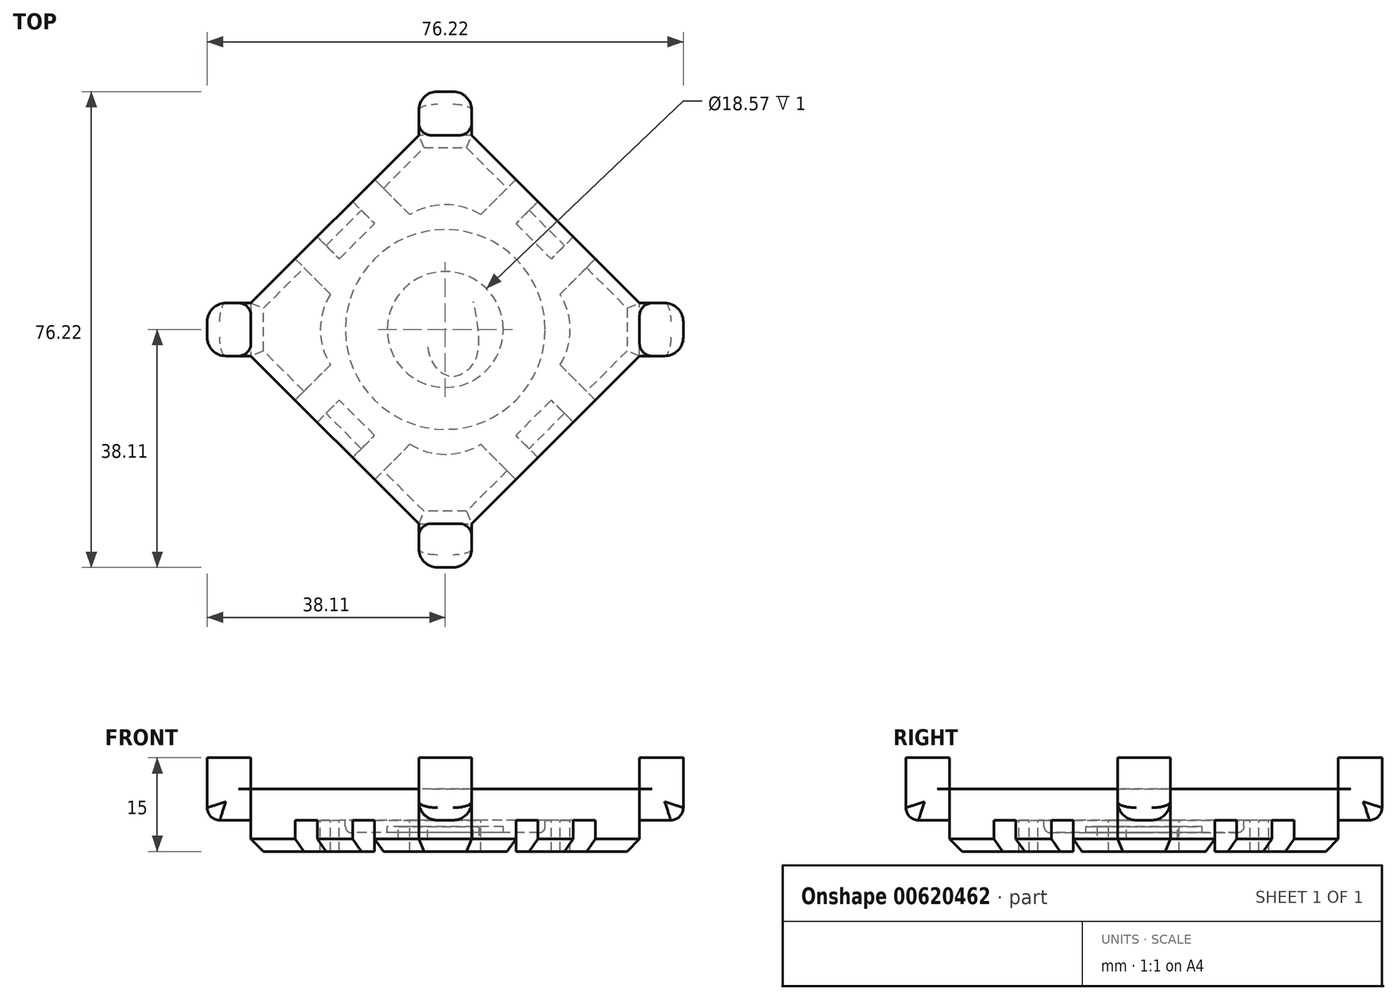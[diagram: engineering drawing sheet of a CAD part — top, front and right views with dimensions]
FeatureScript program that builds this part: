
annotation { "Feature Type Name" : "Feature", "Feature Type Description" : "" }
export const myFeature = defineFeature(function(context is Context, id is Id, definition is map)
    precondition{}
    {
        {
            var Q0;
            Q0=qCreatedBy(makeId("Top.planeOp"),FACE);
            var sketch = newSketch(context, id + "F0", { "sketchPlane" : qUnion([Q0])});
            skLineSegment(sketch, "E0", {"start": v(0, 35.36) * mm, "end": v(0, -35.4) * mm, "construction": true});
            skLineSegment(sketch, "E1", {"start": v(-35.36, 0) * mm, "end": v(35.4, 0) * mm, "construction": true});
            skPoint(sketch, "E2", {"position": v(0, 27.5) * mm});
            skPoint(sketch, "E3", {"position": v(-27.5, 0) * mm});
            skPoint(sketch, "E4", {"position": v(0, -27.5) * mm});
            skPoint(sketch, "E5", {"position": v(27.5, 0) * mm});
            skPoint(sketch, "E6", {"position": v(0, 0) * mm});
            skPoint(sketch, "E7", {"position": v(4.24, 31.11) * mm});
            skPoint(sketch, "E8", {"position": v(-4.24, 31.11) * mm});
            skPoint(sketch, "E9", {"position": v(31.11, 4.24) * mm});
            skPoint(sketch, "E10", {"position": v(31.11, -4.24) * mm});
            skPoint(sketch, "E11", {"position": v(-31.11, -4.24) * mm});
            skPoint(sketch, "E12", {"position": v(-31.11, 4.24) * mm});
            skPoint(sketch, "E13", {"position": v(4.24, -31.11) * mm});
            skPoint(sketch, "E14", {"position": v(-4.24, -31.11) * mm});
            skLineSegment(sketch, "E15", {"start": v(-31.11, 4.24) * mm, "end": v(-4.24, 31.11) * mm});
            skLineSegment(sketch, "E16", {"start": v(4.24, 31.11) * mm, "end": v(31.11, 4.24) * mm});
            skLineSegment(sketch, "E17", {"start": v(31.11, -4.24) * mm, "end": v(4.24, -31.11) * mm});
            skLineSegment(sketch, "E18", {"start": v(-4.24, -31.11) * mm, "end": v(-31.11, -4.24) * mm});
            skLineSegment(sketch, "E19", {"start": v(31.11, 4.24) * mm, "end": v(38.11, 4.24) * mm});
            skLineSegment(sketch, "E20", {"start": v(38.11, 4.24) * mm, "end": v(38.11, -4.24) * mm});
            skLineSegment(sketch, "E21", {"start": v(38.11, -4.24) * mm, "end": v(31.11, -4.24) * mm});
            skLineSegment(sketch, "E22", {"start": v(4.24, -31.11) * mm, "end": v(4.24, -38.11) * mm});
            skLineSegment(sketch, "E23", {"start": v(4.24, -38.11) * mm, "end": v(-4.24, -38.11) * mm});
            skLineSegment(sketch, "E24", {"start": v(-4.24, -38.11) * mm, "end": v(-4.24, -31.11) * mm});
            skLineSegment(sketch, "E25", {"start": v(-31.11, -4.24) * mm, "end": v(-38.11, -4.24) * mm});
            skLineSegment(sketch, "E26", {"start": v(-38.11, -4.24) * mm, "end": v(-38.11, 4.24) * mm});
            skLineSegment(sketch, "E27", {"start": v(-38.11, 4.24) * mm, "end": v(-31.11, 4.24) * mm});
            skLineSegment(sketch, "E28", {"start": v(-4.24, 31.11) * mm, "end": v(-4.24, 38.11) * mm});
            skLineSegment(sketch, "E29", {"start": v(-4.24, 38.11) * mm, "end": v(4.24, 38.11) * mm});
            skLineSegment(sketch, "E30", {"start": v(4.24, 38.11) * mm, "end": v(4.24, 31.11) * mm});
            skLineSegment(sketch, "E31", {"start": v(-4.24, -31.11) * mm, "end": v(4.24, -31.11) * mm});
            skLineSegment(sketch, "E32", {"start": v(31.11, -4.24) * mm, "end": v(31.11, 4.24) * mm});
            skLineSegment(sketch, "E33", {"start": v(4.24, 31.11) * mm, "end": v(-4.24, 31.11) * mm});
            skLineSegment(sketch, "E34", {"start": v(-31.11, 4.24) * mm, "end": v(-31.11, -4.24) * mm});
            skPoint(sketch, "E35", {"position": v(11.31, 24.04) * mm});
            skPoint(sketch, "E36", {"position": v(14.85, 20.5) * mm});
            skPoint(sketch, "E37", {"position": v(20.5, 14.85) * mm});
            skPoint(sketch, "E38", {"position": v(24.04, 11.31) * mm});
            skPoint(sketch, "E39", {"position": v(-24.04, -11.31) * mm});
            skPoint(sketch, "E40", {"position": v(-20.5, -14.85) * mm});
            skPoint(sketch, "E41", {"position": v(-14.85, -20.5) * mm});
            skPoint(sketch, "E42", {"position": v(-11.31, -24.04) * mm});
            skPoint(sketch, "E43", {"position": v(11.31, -24.04) * mm});
            skPoint(sketch, "E44", {"position": v(14.85, -20.5) * mm});
            skPoint(sketch, "E45", {"position": v(20.5, -14.85) * mm});
            skPoint(sketch, "E46", {"position": v(24.04, -11.31) * mm});
            skPoint(sketch, "E47", {"position": v(-24.04, 11.31) * mm});
            skPoint(sketch, "E48", {"position": v(-20.5, 14.85) * mm});
            skPoint(sketch, "E49", {"position": v(-14.85, 20.5) * mm});
            skPoint(sketch, "E50", {"position": v(-11.31, 24.04) * mm});
            skLineSegment(sketch, "E51", {"start": v(-24.04, -11.31) * mm, "end": v(-18.38, -5.66) * mm});
            skLineSegment(sketch, "E52", {"start": v(-24.04, 11.31) * mm, "end": v(-18.38, 5.66) * mm});
            skLineSegment(sketch, "E53", {"start": v(-20.5, 14.85) * mm, "end": v(-16.97, 11.31) * mm});
            skLineSegment(sketch, "E54", {"start": v(-14.85, 20.5) * mm, "end": v(-11.31, 16.97) * mm});
            skLineSegment(sketch, "E55", {"start": v(-11.31, 24.04) * mm, "end": v(-5.66, 18.38) * mm});
            skLineSegment(sketch, "E56", {"start": v(11.31, 24.04) * mm, "end": v(5.66, 18.38) * mm});
            skLineSegment(sketch, "E57", {"start": v(14.85, 20.5) * mm, "end": v(11.31, 16.97) * mm});
            skLineSegment(sketch, "E58", {"start": v(20.5, 14.85) * mm, "end": v(16.97, 11.31) * mm});
            skLineSegment(sketch, "E59", {"start": v(24.04, 11.31) * mm, "end": v(18.39, 5.66) * mm});
            skLineSegment(sketch, "E60", {"start": v(24.04, -11.31) * mm, "end": v(18.38, -5.66) * mm});
            skLineSegment(sketch, "E61", {"start": v(20.5, -14.85) * mm, "end": v(16.97, -11.31) * mm});
            skLineSegment(sketch, "E62", {"start": v(11.31, -24.04) * mm, "end": v(5.66, -18.38) * mm});
            skLineSegment(sketch, "E63", {"start": v(14.85, -20.5) * mm, "end": v(11.31, -16.97) * mm});
            skLineSegment(sketch, "E64", {"start": v(-20.5, -14.85) * mm, "end": v(-16.97, -11.31) * mm});
            skLineSegment(sketch, "E65", {"start": v(-14.85, -20.5) * mm, "end": v(-11.31, -16.97) * mm});
            skLineSegment(sketch, "E66", {"start": v(-11.31, -24.04) * mm, "end": v(-5.66, -18.38) * mm});
            skLineSegment(sketch, "E67", {"start": v(-16.97, 11.31) * mm, "end": v(-11.31, 16.97) * mm});
            skLineSegment(sketch, "E68", {"start": v(11.31, 16.97) * mm, "end": v(16.97, 11.31) * mm});
            skLineSegment(sketch, "E69", {"start": v(16.97, -11.31) * mm, "end": v(11.31, -16.97) * mm});
            skLineSegment(sketch, "E70", {"start": v(-11.31, -16.97) * mm, "end": v(-16.97, -11.31) * mm});
            skPoint(sketch, "E71", {"position": v(-20, 0) * mm});
            skPoint(sketch, "E72", {"position": v(0, -20) * mm});
            skPoint(sketch, "E73", {"position": v(20, 0) * mm});
            skPoint(sketch, "E74", {"position": v(0, 20) * mm});
            skArc(sketch, "E75", {"start": v(-18.38, 5.66) * mm, "mid": v(-20, 0) * mm, "end": v(-18.38, -5.66) * mm});
            skArc(sketch, "E76", {"start": v(-5.66, -18.38) * mm, "mid": v(0, -20) * mm, "end": v(5.66, -18.38) * mm});
            skArc(sketch, "E77", {"start": v(18.38, -5.66) * mm, "mid": v(20, 0) * mm, "end": v(18.39, 5.66) * mm});
            skArc(sketch, "E78", {"start": v(5.66, 18.38) * mm, "mid": v(0, 20) * mm, "end": v(-5.66, 18.38) * mm});
            skCircle(sketch, "E79", {"center": v(0, 0) * mm, "radius": 16 * mm});
            skCircle(sketch, "E80", {"center": v(0, 0) * mm, "radius": 9.29 * mm});
            skLineSegment(sketch, "E81", {"start": v(0, 0) * mm, "end": v(-6.57, -6.57) * mm, "construction": true});
            skLineSegment(sketch, "E82", {"start": v(0, 0) * mm, "end": v(6.57, 6.57) * mm, "construction": true});
            skPoint(sketch, "E83", {"position": v(-2.83, -2.83) * mm});
            skPoint(sketch, "E84", {"position": v(4.45, 4.45) * mm});
            skFitSpline(sketch, "E85", {"points": [v(-2.83, -2.83) * mm, v(-5.25, -2.1) * mm, v(-7.48, 0.8) * mm, v(-5.7, 4.36) * mm, v(-1.66, 5.38) * mm, v(2.42, 4.94) * mm, v(4.45, 4.45) * mm], "startDerivative": vector(-16.37, 2.6) * mm, "endDerivative": vector(12.64, -5.97) * mm});
            skFitSpline(sketch, "E86.MirrorCS", {"points": [v(-2.83, -2.83) * mm, v(-2.1, -5.25) * mm, v(0.8, -7.48) * mm, v(4.36, -5.7) * mm, v(5.38, -1.66) * mm, v(4.94, 2.42) * mm, v(4.45, 4.45) * mm], "startDerivative": vector(2.6, -16.37) * mm, "endDerivative": vector(-5.97, 12.64) * mm});
            skSolve(sketch);
        }
        {
            var Q0;
            {var subQ19=sQuery(id+"F0.wireOp",EDGE,"E51");Q0=makeQuery(id+"F0.imprint","IMPRINT",FACE,{"disambiguationData":[TD([[makeQuery(id+"F0.imprint","IMPRINT",EDGE,{"derivedFrom":subQ19}),-1.0]])]});}
            var Q1;
            Q1=makeQuery(id+"F0.imprint","IMPRINT",FACE,{"disambiguationData":[TD([[makeQuery(id+"F0.imprint","IMPRINT",EDGE,{"derivedFrom":sQuery(id+"F0.wireOp",EDGE,"E19")}),-1.0]])]});
            var Q2;
            {var subQ0=sQuery(id+"F0.wireOp",EDGE,"E64");Q2=makeQuery(id+"F0.imprint","IMPRINT",FACE,{"disambiguationData":[TD([[makeQuery(id+"F0.imprint","IMPRINT",EDGE,{"derivedFrom":subQ0}),-1.0]])]});}
            var Q3;
            Q3=makeQuery(id+"F0.imprint","IMPRINT",FACE,{"disambiguationData":[TD([[makeQuery(id+"F0.imprint","IMPRINT",EDGE,{"derivedFrom":sQuery(id+"F0.wireOp",EDGE,"E34")}),-1.0]])]});
            var Q4;
            Q4=makeQuery(id+"F0.imprint","IMPRINT",FACE,{"disambiguationData":[TD([[makeQuery(id+"F0.imprint","IMPRINT",EDGE,{"derivedFrom":sQuery(id+"F0.wireOp",EDGE,"E31")}),-1.0]])]});
            var Q5;
            Q5=makeQuery(id+"F0.imprint","IMPRINT",FACE,{"disambiguationData":[TD([[makeQuery(id+"F0.imprint","IMPRINT",EDGE,{"derivedFrom":sQuery(id+"F0.wireOp",EDGE,"E32")}),-1.0]])]});
            var Q6;
            {var subQ0=sQuery(id+"F0.wireOp",EDGE,"E57");Q6=makeQuery(id+"F0.imprint","IMPRINT",FACE,{"disambiguationData":[TD([[makeQuery(id+"F0.imprint","IMPRINT",EDGE,{"derivedFrom":subQ0}),1.0]])]});}
            var Q7;
            {var subQ1=sQuery(id+"F0.wireOp",EDGE,"E33");Q7=makeQuery(id+"F0.imprint","IMPRINT",FACE,{"disambiguationData":[TD([[makeQuery(id+"F0.imprint","IMPRINT",EDGE,{"derivedFrom":subQ1}),1.0]])]});}
            var Q8;
            {var subQ1=sQuery(id+"F0.wireOp",EDGE,"E32");Q8=makeQuery(id+"F0.imprint","IMPRINT",FACE,{"disambiguationData":[TD([[makeQuery(id+"F0.imprint","IMPRINT",EDGE,{"derivedFrom":subQ1}),1.0]])]});}
            var Q9;
            Q9=makeQuery(id+"F0.imprint","IMPRINT",FACE,{"disambiguationData":[TD([[makeQuery(id+"F0.imprint","IMPRINT",EDGE,{"derivedFrom":sQuery(id+"F0.wireOp",EDGE,"E33")}),-1.0]])]});
            var Q10;
            {var subQ1=sQuery(id+"F0.wireOp",EDGE,"E34");Q10=makeQuery(id+"F0.imprint","IMPRINT",FACE,{"disambiguationData":[TD([[makeQuery(id+"F0.imprint","IMPRINT",EDGE,{"derivedFrom":subQ1}),1.0]])]});}
            var Q11;
            {var subQ1=sQuery(id+"F0.wireOp",EDGE,"E31");Q11=makeQuery(id+"F0.imprint","IMPRINT",FACE,{"disambiguationData":[TD([[makeQuery(id+"F0.imprint","IMPRINT",EDGE,{"derivedFrom":subQ1}),1.0]])]});}
            var Q12;
            Q12=makeQuery(id+"F0.imprint","IMPRINT",FACE,{"disambiguationData":[TD([[makeQuery(id+"F0.imprint","IMPRINT",EDGE,{"derivedFrom":sQuery(id+"F0.wireOp",EDGE,"E25")}),-1.0]])]});
            var Q13;
            Q13=makeQuery(id+"F0.imprint","IMPRINT",FACE,{"disambiguationData":[TD([[makeQuery(id+"F0.imprint","IMPRINT",EDGE,{"derivedFrom":sQuery(id+"F0.wireOp",EDGE,"E28")}),-1.0]])]});
            var Q14;
            Q14=makeQuery(id+"F0.imprint","IMPRINT",FACE,{"disambiguationData":[TD([[makeQuery(id+"F0.imprint","IMPRINT",EDGE,{"derivedFrom":sQuery(id+"F0.wireOp",EDGE,"E22")}),-1.0]])]});
            var Q15;
            {var subQ0=sQuery(id+"F0.wireOp",EDGE,"E53");Q15=makeQuery(id+"F0.imprint","IMPRINT",FACE,{"disambiguationData":[TD([[makeQuery(id+"F0.imprint","IMPRINT",EDGE,{"derivedFrom":subQ0}),1.0]])]});}
            var Q16;
            {var subQ0=sQuery(id+"F0.wireOp",EDGE,"E61");Q16=makeQuery(id+"F0.imprint","IMPRINT",FACE,{"disambiguationData":[TD([[makeQuery(id+"F0.imprint","IMPRINT",EDGE,{"derivedFrom":subQ0}),1.0]])]});}
            extrude(context, id + "F1", {"entities" : qUnion([Q0, Q1, Q2, Q3, Q4, Q5, Q6, Q7, Q8, Q9, Q10, Q11, Q12, Q13, Q14, Q15, Q16]), "oppositeDirection" : true, "depth" : 5 * mm, "offsetDistance" : 25 * mm});
        }
        {
            var Q0;
            Q0=makeQuery(id+"F0.imprint","IMPRINT",FACE,{"disambiguationData":[TD([[makeQuery(id+"F0.imprint","IMPRINT",EDGE,{"derivedFrom":sQuery(id+"F0.wireOp",EDGE,"E25")}),-1.0]])]});
            var Q1;
            Q1=makeQuery(id+"F0.imprint","IMPRINT",FACE,{"disambiguationData":[TD([[makeQuery(id+"F0.imprint","IMPRINT",EDGE,{"derivedFrom":sQuery(id+"F0.wireOp",EDGE,"E28")}),-1.0]])]});
            var Q2;
            Q2=makeQuery(id+"F0.imprint","IMPRINT",FACE,{"disambiguationData":[TD([[makeQuery(id+"F0.imprint","IMPRINT",EDGE,{"derivedFrom":sQuery(id+"F0.wireOp",EDGE,"E19")}),-1.0]])]});
            var Q3;
            Q3=makeQuery(id+"F0.imprint","IMPRINT",FACE,{"disambiguationData":[TD([[makeQuery(id+"F0.imprint","IMPRINT",EDGE,{"derivedFrom":sQuery(id+"F0.wireOp",EDGE,"E22")}),-1.0]])]});
            extrude(context, id + "F2", {"entities" : qUnion([Q0, Q1, Q2, Q3]), "operationType" : NewBodyOperationType.ADD, "depth" : 5 * mm, "offsetDistance" : 25 * mm});
        }
        {
            var Q0;
            {var subQ1=sQuery(id+"F0.wireOp",EDGE,"E34");Q0=makeQuery(id+"F0.imprint","IMPRINT",FACE,{"disambiguationData":[TD([[makeQuery(id+"F0.imprint","IMPRINT",EDGE,{"derivedFrom":subQ1}),1.0]])]});}
            var Q1;
            {var subQ0=sQuery(id+"F0.wireOp",EDGE,"E53");Q1=makeQuery(id+"F0.imprint","IMPRINT",FACE,{"disambiguationData":[TD([[makeQuery(id+"F0.imprint","IMPRINT",EDGE,{"derivedFrom":subQ0}),1.0]])]});}
            var Q2;
            {var subQ1=sQuery(id+"F0.wireOp",EDGE,"E33");Q2=makeQuery(id+"F0.imprint","IMPRINT",FACE,{"disambiguationData":[TD([[makeQuery(id+"F0.imprint","IMPRINT",EDGE,{"derivedFrom":subQ1}),1.0]])]});}
            var Q3;
            {var subQ0=sQuery(id+"F0.wireOp",EDGE,"E57");Q3=makeQuery(id+"F0.imprint","IMPRINT",FACE,{"disambiguationData":[TD([[makeQuery(id+"F0.imprint","IMPRINT",EDGE,{"derivedFrom":subQ0}),1.0]])]});}
            var Q4;
            {var subQ1=sQuery(id+"F0.wireOp",EDGE,"E32");Q4=makeQuery(id+"F0.imprint","IMPRINT",FACE,{"disambiguationData":[TD([[makeQuery(id+"F0.imprint","IMPRINT",EDGE,{"derivedFrom":subQ1}),1.0]])]});}
            var Q5;
            {var subQ0=sQuery(id+"F0.wireOp",EDGE,"E61");Q5=makeQuery(id+"F0.imprint","IMPRINT",FACE,{"disambiguationData":[TD([[makeQuery(id+"F0.imprint","IMPRINT",EDGE,{"derivedFrom":subQ0}),1.0]])]});}
            var Q6;
            {var subQ1=sQuery(id+"F0.wireOp",EDGE,"E31");Q6=makeQuery(id+"F0.imprint","IMPRINT",FACE,{"disambiguationData":[TD([[makeQuery(id+"F0.imprint","IMPRINT",EDGE,{"derivedFrom":subQ1}),1.0]])]});}
            var Q7;
            {var subQ0=sQuery(id+"F0.wireOp",EDGE,"E64");Q7=makeQuery(id+"F0.imprint","IMPRINT",FACE,{"disambiguationData":[TD([[makeQuery(id+"F0.imprint","IMPRINT",EDGE,{"derivedFrom":subQ0}),-1.0]])]});}
            extrude(context, id + "F3", {"entities" : qUnion([Q0, Q1, Q2, Q3, Q4, Q5, Q6, Q7]), "operationType" : NewBodyOperationType.ADD, "oppositeDirection" : true, "depth" : 10 * mm, "offsetDistance" : 25 * mm});
        }
        {
            var Q0;
            Q0=makeQuery(id+"F1.opExtrude","CAP_EDGE",EDGE,{"disambiguationData":[OSD([sQuery(id+"F0.wireOp",EDGE,"E26")])],"isStart":false});
            var Q1;
            Q1=makeQuery(id+"F1.opExtrude","CAP_EDGE",EDGE,{"disambiguationData":[OSD([sQuery(id+"F0.wireOp",EDGE,"E23")])],"isStart":false});
            var Q2;
            Q2=makeQuery(id+"F1.opExtrude","CAP_EDGE",EDGE,{"disambiguationData":[OSD([sQuery(id+"F0.wireOp",EDGE,"E20")])],"isStart":false});
            var Q3;
            Q3=makeQuery(id+"F1.opExtrude","CAP_EDGE",EDGE,{"disambiguationData":[OSD([sQuery(id+"F0.wireOp",EDGE,"E29")])],"isStart":false});
            fillet(context, id + "F4", {"entities" : qUnion([Q0, Q1, Q2, Q3]), "radius" : 2 * mm, "tangentPropagation" : true, "allowEdgeOverflow" : false});
        }
        {
            var Q0;
            {var subQ0=sQuery(id+"F0.wireOp",EDGE,"E27");var subQ1=sQuery(id+"F0.wireOp",EDGE,"E26");Q0=makeQuery(id+"F2.boolean.opBoolean","MERGE",EDGE,{"derivedFrom":[makeQuery(id+"F1.opExtrude","SWEPT_EDGE",EDGE,{"disambiguationData":[OSD([subQ1,subQ0])]}),makeQuery(id+"F2.opExtrude","SWEPT_EDGE",EDGE,{"disambiguationData":[OSD([subQ1,subQ0])]})]});}
            var Q1;
            {var subQ0=sQuery(id+"F0.wireOp",EDGE,"E26");var subQ1=sQuery(id+"F0.wireOp",EDGE,"E25");Q1=makeQuery(id+"F2.boolean.opBoolean","MERGE",EDGE,{"derivedFrom":[makeQuery(id+"F1.opExtrude","SWEPT_EDGE",EDGE,{"disambiguationData":[OSD([subQ1,subQ0])]}),makeQuery(id+"F2.opExtrude","SWEPT_EDGE",EDGE,{"disambiguationData":[OSD([subQ1,subQ0])]})]});}
            var Q2;
            {var subQ0=sQuery(id+"F0.wireOp",EDGE,"E24");var subQ1=sQuery(id+"F0.wireOp",EDGE,"E23");Q2=makeQuery(id+"F2.boolean.opBoolean","MERGE",EDGE,{"derivedFrom":[makeQuery(id+"F1.opExtrude","SWEPT_EDGE",EDGE,{"disambiguationData":[OSD([subQ1,subQ0])]}),makeQuery(id+"F2.opExtrude","SWEPT_EDGE",EDGE,{"disambiguationData":[OSD([subQ1,subQ0])]})]});}
            var Q3;
            {var subQ0=sQuery(id+"F0.wireOp",EDGE,"E23");var subQ1=sQuery(id+"F0.wireOp",EDGE,"E22");Q3=makeQuery(id+"F2.boolean.opBoolean","MERGE",EDGE,{"derivedFrom":[makeQuery(id+"F1.opExtrude","SWEPT_EDGE",EDGE,{"disambiguationData":[OSD([subQ1,subQ0])]}),makeQuery(id+"F2.opExtrude","SWEPT_EDGE",EDGE,{"disambiguationData":[OSD([subQ1,subQ0])]})]});}
            var Q4;
            {var subQ0=sQuery(id+"F0.wireOp",EDGE,"E21");var subQ1=sQuery(id+"F0.wireOp",EDGE,"E20");Q4=makeQuery(id+"F2.boolean.opBoolean","MERGE",EDGE,{"derivedFrom":[makeQuery(id+"F1.opExtrude","SWEPT_EDGE",EDGE,{"disambiguationData":[OSD([subQ1,subQ0])]}),makeQuery(id+"F2.opExtrude","SWEPT_EDGE",EDGE,{"disambiguationData":[OSD([subQ1,subQ0])]})]});}
            var Q5;
            {var subQ0=sQuery(id+"F0.wireOp",EDGE,"E20");var subQ1=sQuery(id+"F0.wireOp",EDGE,"E19");Q5=makeQuery(id+"F2.boolean.opBoolean","MERGE",EDGE,{"derivedFrom":[makeQuery(id+"F1.opExtrude","SWEPT_EDGE",EDGE,{"disambiguationData":[OSD([subQ1,subQ0])]}),makeQuery(id+"F2.opExtrude","SWEPT_EDGE",EDGE,{"disambiguationData":[OSD([subQ1,subQ0])]})]});}
            var Q6;
            {var subQ0=sQuery(id+"F0.wireOp",EDGE,"E30");var subQ1=sQuery(id+"F0.wireOp",EDGE,"E29");Q6=makeQuery(id+"F2.boolean.opBoolean","MERGE",EDGE,{"derivedFrom":[makeQuery(id+"F1.opExtrude","SWEPT_EDGE",EDGE,{"disambiguationData":[OSD([subQ1,subQ0])]}),makeQuery(id+"F2.opExtrude","SWEPT_EDGE",EDGE,{"disambiguationData":[OSD([subQ1,subQ0])]})]});}
            var Q7;
            {var subQ0=sQuery(id+"F0.wireOp",EDGE,"E29");var subQ1=sQuery(id+"F0.wireOp",EDGE,"E28");Q7=makeQuery(id+"F2.boolean.opBoolean","MERGE",EDGE,{"derivedFrom":[makeQuery(id+"F1.opExtrude","SWEPT_EDGE",EDGE,{"disambiguationData":[OSD([subQ1,subQ0])]}),makeQuery(id+"F2.opExtrude","SWEPT_EDGE",EDGE,{"disambiguationData":[OSD([subQ1,subQ0])]})]});}
            fillet(context, id + "F5", {"entities" : qUnion([Q0, Q1, Q2, Q3, Q4, Q5, Q6, Q7]), "radius" : 3 * mm, "tangentPropagation" : true, "allowEdgeOverflow" : false});
        }
        {
            var Q0;
            Q0=makeQuery(id+"F2.opExtrude","SWEPT_EDGE",EDGE,{"disambiguationData":[OSD([sQuery(id+"F0.wireOp",EDGE,"E15"),sQuery(id+"F0.wireOp",EDGE,"E27"),sQuery(id+"F0.wireOp",EDGE,"E34"),sQuery(id+"F0.wireOp",EDGE,"GMtcQSGh-03BE-9S7f-jexl-TCLt15MjE30i")])]});
            var Q1;
            Q1=makeQuery(id+"F2.opExtrude","SWEPT_EDGE",EDGE,{"disambiguationData":[OSD([sQuery(id+"F0.wireOp",EDGE,"E18"),sQuery(id+"F0.wireOp",EDGE,"E25"),sQuery(id+"F0.wireOp",EDGE,"E34"),sQuery(id+"F0.wireOp",EDGE,"GMtcQSGh-03BE-9S7f-jexl-TCLt15MjE30i")])]});
            var Q2;
            Q2=makeQuery(id+"F2.opExtrude","SWEPT_EDGE",EDGE,{"disambiguationData":[OSD([sQuery(id+"F0.wireOp",EDGE,"E15"),sQuery(id+"F0.wireOp",EDGE,"E28"),sQuery(id+"F0.wireOp",EDGE,"E33"),sQuery(id+"F0.wireOp",EDGE,"3PBwVQnR-xdhY-csVz-Pc8j-sIx2GhVsqBVA")])]});
            var Q3;
            Q3=makeQuery(id+"F2.opExtrude","SWEPT_EDGE",EDGE,{"disambiguationData":[OSD([sQuery(id+"F0.wireOp",EDGE,"E16"),sQuery(id+"F0.wireOp",EDGE,"E30"),sQuery(id+"F0.wireOp",EDGE,"E33"),sQuery(id+"F0.wireOp",EDGE,"3PBwVQnR-xdhY-csVz-Pc8j-sIx2GhVsqBVA")])]});
            var Q4;
            Q4=makeQuery(id+"F2.opExtrude","SWEPT_EDGE",EDGE,{"disambiguationData":[OSD([sQuery(id+"F0.wireOp",EDGE,"E17"),sQuery(id+"F0.wireOp",EDGE,"E22"),sQuery(id+"F0.wireOp",EDGE,"E31"),sQuery(id+"F0.wireOp",EDGE,"QYXsK6sv-4NLd-NN4k-doHg-mYEpJDkLXwFN")])]});
            var Q5;
            Q5=makeQuery(id+"F2.opExtrude","SWEPT_EDGE",EDGE,{"disambiguationData":[OSD([sQuery(id+"F0.wireOp",EDGE,"E18"),sQuery(id+"F0.wireOp",EDGE,"E24"),sQuery(id+"F0.wireOp",EDGE,"E31"),sQuery(id+"F0.wireOp",EDGE,"QYXsK6sv-4NLd-NN4k-doHg-mYEpJDkLXwFN")])]});
            var Q6;
            Q6=makeQuery(id+"F2.opExtrude","SWEPT_EDGE",EDGE,{"disambiguationData":[OSD([sQuery(id+"F0.wireOp",EDGE,"E17"),sQuery(id+"F0.wireOp",EDGE,"E21"),sQuery(id+"F0.wireOp",EDGE,"E32"),sQuery(id+"F0.wireOp",EDGE,"Ge9slQAG-61Rj-s7dv-aatR-5Ow67fPWWa0J")])]});
            var Q7;
            Q7=makeQuery(id+"F2.opExtrude","SWEPT_EDGE",EDGE,{"disambiguationData":[OSD([sQuery(id+"F0.wireOp",EDGE,"E16"),sQuery(id+"F0.wireOp",EDGE,"E19"),sQuery(id+"F0.wireOp",EDGE,"E32"),sQuery(id+"F0.wireOp",EDGE,"Ge9slQAG-61Rj-s7dv-aatR-5Ow67fPWWa0J")])]});
            fillet(context, id + "F6", {"entities" : qUnion([Q0, Q1, Q2, Q3, Q4, Q5, Q6, Q7]), "radius" : 2 * mm, "tangentPropagation" : true, "allowEdgeOverflow" : false});
        }
        {
            var Q0;
            Q0=makeQuery(id+"F0.imprint","IMPRINT",FACE,{"disambiguationData":[TD([[makeQuery(id+"F0.imprint","IMPRINT",EDGE,{"derivedFrom":sQuery(id+"F0.wireOp",EDGE,"E79")}),1.0]])]});
            extrude(context, id + "F7", {"entities" : qUnion([Q0]), "operationType" : NewBodyOperationType.ADD, "oppositeDirection" : true, "depth" : 7 * mm, "offsetDistance" : 25 * mm});
        }
        {
            var Q0;
            Q0=makeQuery(id+"F0.imprint","IMPRINT",FACE,{"disambiguationData":[TD([[makeQuery(id+"F0.imprint","IMPRINT",EDGE,{"derivedFrom":sQuery(id+"F0.wireOp",EDGE,"E80")}),1.0]])]});
            extrude(context, id + "F8", {"entities" : qUnion([Q0]), "operationType" : NewBodyOperationType.ADD, "oppositeDirection" : true, "depth" : 6 * mm, "offsetDistance" : 25 * mm});
        }
        {
            var Q0;
            Q0=makeQuery(id+"F0.imprint","IMPRINT",FACE,{"disambiguationData":[TD([[makeQuery(id+"F0.imprint","IMPRINT",EDGE,{"derivedFrom":sQuery(id+"F0.wireOp",EDGE,"E85")}),-1.0]])]});
            extrude(context, id + "F9", {"entities" : qUnion([Q0]), "operationType" : NewBodyOperationType.ADD, "oppositeDirection" : true, "depth" : 8 * mm, "offsetDistance" : 25 * mm});
        }
        {
            var Q0;
            Q0=makeQuery(id+"F7.opExtrude","CAP_EDGE",EDGE,{"disambiguationData":[OSD([sQuery(id+"F0.wireOp",EDGE,"E79")])],"isStart":false});
            fillet(context, id + "F10", {"entities" : qUnion([Q0]), "radius" : 1 * mm, "tangentPropagation" : true, "allowEdgeOverflow" : false});
        }
        {
            var Q0;
            {var subQ0=sQuery(id+"F0.wireOp",EDGE,"E15");Q0=makeQuery(id+"F3.opExtrude","CAP_EDGE",EDGE,{"disambiguationData":[OSD([subQ0]),TDD([makeQuery(id+"F0.imprint","IMPRINT",EDGE,{"disambiguationData":[TD([[makeQuery(id+"F0.imprint","INTERSECT",VERTEX,{"derivedFrom":[subQ0,sQuery(id+"F0.wireOp",EDGE,"E53")]}),-1.0]])],"derivedFrom":subQ0})])],"isStart":false});}
            var Q1;
            {var subQ0=sQuery(id+"F0.wireOp",EDGE,"E15");Q1=makeQuery(id+"F3.opExtrude","CAP_EDGE",EDGE,{"disambiguationData":[OSD([subQ0]),TDD([makeQuery(id+"F0.imprint","IMPRINT",EDGE,{"disambiguationData":[TD([[makeQuery(id+"F0.imprint","INTERSECT",VERTEX,{"derivedFrom":[subQ0,sQuery(id+"F0.wireOp",EDGE,"E52")]}),1.0]])],"derivedFrom":subQ0})])],"isStart":false});}
            var Q2;
            Q2=makeQuery(id+"F3.opExtrude","CAP_EDGE",EDGE,{"disambiguationData":[OSD([sQuery(id+"F0.wireOp",EDGE,"E34")])],"isStart":false});
            var Q3;
            {var subQ0=sQuery(id+"F0.wireOp",EDGE,"E18");Q3=makeQuery(id+"F3.opExtrude","CAP_EDGE",EDGE,{"disambiguationData":[OSD([subQ0]),TDD([makeQuery(id+"F0.imprint","IMPRINT",EDGE,{"disambiguationData":[TD([[makeQuery(id+"F0.imprint","INTERSECT",VERTEX,{"derivedFrom":[subQ0,sQuery(id+"F0.wireOp",EDGE,"E51")]}),-1.0]])],"derivedFrom":subQ0})])],"isStart":false});}
            var Q4;
            {var subQ0=sQuery(id+"F0.wireOp",EDGE,"E18");Q4=makeQuery(id+"F3.opExtrude","CAP_EDGE",EDGE,{"disambiguationData":[OSD([subQ0]),TDD([makeQuery(id+"F0.imprint","IMPRINT",EDGE,{"disambiguationData":[TD([[makeQuery(id+"F0.imprint","INTERSECT",VERTEX,{"derivedFrom":[subQ0,sQuery(id+"F0.wireOp",EDGE,"E64")]}),1.0]])],"derivedFrom":subQ0})])],"isStart":false});}
            var Q5;
            {var subQ0=sQuery(id+"F0.wireOp",EDGE,"E18");Q5=makeQuery(id+"F3.opExtrude","CAP_EDGE",EDGE,{"disambiguationData":[OSD([subQ0]),TDD([makeQuery(id+"F0.imprint","IMPRINT",EDGE,{"disambiguationData":[TD([[makeQuery(id+"F0.imprint","INTERSECT",VERTEX,{"derivedFrom":[subQ0,sQuery(id+"F0.wireOp",EDGE,"E66")]}),1.0]])],"derivedFrom":subQ0})])],"isStart":false});}
            var Q6;
            Q6=makeQuery(id+"F3.opExtrude","CAP_EDGE",EDGE,{"disambiguationData":[OSD([sQuery(id+"F0.wireOp",EDGE,"E31")])],"isStart":false});
            var Q7;
            {var subQ0=sQuery(id+"F0.wireOp",EDGE,"E17");Q7=makeQuery(id+"F3.opExtrude","CAP_EDGE",EDGE,{"disambiguationData":[OSD([subQ0]),TDD([makeQuery(id+"F0.imprint","IMPRINT",EDGE,{"disambiguationData":[TD([[makeQuery(id+"F0.imprint","INTERSECT",VERTEX,{"derivedFrom":[subQ0,sQuery(id+"F0.wireOp",EDGE,"E62")]}),-1.0]])],"derivedFrom":subQ0})])],"isStart":false});}
            var Q8;
            {var subQ0=sQuery(id+"F0.wireOp",EDGE,"E17");Q8=makeQuery(id+"F3.opExtrude","CAP_EDGE",EDGE,{"disambiguationData":[OSD([subQ0]),TDD([makeQuery(id+"F0.imprint","IMPRINT",EDGE,{"disambiguationData":[TD([[makeQuery(id+"F0.imprint","INTERSECT",VERTEX,{"derivedFrom":[subQ0,sQuery(id+"F0.wireOp",EDGE,"E61")]}),-1.0]])],"derivedFrom":subQ0})])],"isStart":false});}
            var Q9;
            {var subQ0=sQuery(id+"F0.wireOp",EDGE,"E17");Q9=makeQuery(id+"F3.opExtrude","CAP_EDGE",EDGE,{"disambiguationData":[OSD([subQ0]),TDD([makeQuery(id+"F0.imprint","IMPRINT",EDGE,{"disambiguationData":[TD([[makeQuery(id+"F0.imprint","INTERSECT",VERTEX,{"derivedFrom":[subQ0,sQuery(id+"F0.wireOp",EDGE,"E60")]}),1.0]])],"derivedFrom":subQ0})])],"isStart":false});}
            var Q10;
            Q10=makeQuery(id+"F3.opExtrude","CAP_EDGE",EDGE,{"disambiguationData":[OSD([sQuery(id+"F0.wireOp",EDGE,"E32")])],"isStart":false});
            var Q11;
            {var subQ0=sQuery(id+"F0.wireOp",EDGE,"E16");Q11=makeQuery(id+"F3.opExtrude","CAP_EDGE",EDGE,{"disambiguationData":[OSD([subQ0]),TDD([makeQuery(id+"F0.imprint","IMPRINT",EDGE,{"disambiguationData":[TD([[makeQuery(id+"F0.imprint","INTERSECT",VERTEX,{"derivedFrom":[subQ0,sQuery(id+"F0.wireOp",EDGE,"E59")]}),-1.0]])],"derivedFrom":subQ0})])],"isStart":false});}
            var Q12;
            {var subQ0=sQuery(id+"F0.wireOp",EDGE,"E16");Q12=makeQuery(id+"F3.opExtrude","CAP_EDGE",EDGE,{"disambiguationData":[OSD([subQ0]),TDD([makeQuery(id+"F0.imprint","IMPRINT",EDGE,{"disambiguationData":[TD([[makeQuery(id+"F0.imprint","INTERSECT",VERTEX,{"derivedFrom":[subQ0,sQuery(id+"F0.wireOp",EDGE,"E57")]}),-1.0]])],"derivedFrom":subQ0})])],"isStart":false});}
            var Q13;
            {var subQ0=sQuery(id+"F0.wireOp",EDGE,"E16");Q13=makeQuery(id+"F3.opExtrude","CAP_EDGE",EDGE,{"disambiguationData":[OSD([subQ0]),TDD([makeQuery(id+"F0.imprint","IMPRINT",EDGE,{"disambiguationData":[TD([[makeQuery(id+"F0.imprint","INTERSECT",VERTEX,{"derivedFrom":[subQ0,sQuery(id+"F0.wireOp",EDGE,"E56")]}),1.0]])],"derivedFrom":subQ0})])],"isStart":false});}
            var Q14;
            Q14=makeQuery(id+"F3.opExtrude","CAP_EDGE",EDGE,{"disambiguationData":[OSD([sQuery(id+"F0.wireOp",EDGE,"E33")])],"isStart":false});
            var Q15;
            {var subQ0=sQuery(id+"F0.wireOp",EDGE,"E15");Q15=makeQuery(id+"F3.opExtrude","CAP_EDGE",EDGE,{"disambiguationData":[OSD([subQ0]),TDD([makeQuery(id+"F0.imprint","IMPRINT",EDGE,{"disambiguationData":[TD([[makeQuery(id+"F0.imprint","INTERSECT",VERTEX,{"derivedFrom":[subQ0,sQuery(id+"F0.wireOp",EDGE,"E55")]}),-1.0]])],"derivedFrom":subQ0})])],"isStart":false});}
            chamfer(context, id + "F11", {"entities" : qUnion([Q0, Q1, Q2, Q3, Q4, Q5, Q6, Q7, Q8, Q9, Q10, Q11, Q12, Q13, Q14, Q15]), "width" : 2 * mm, "tangentPropagation" : true});
        }
    });
